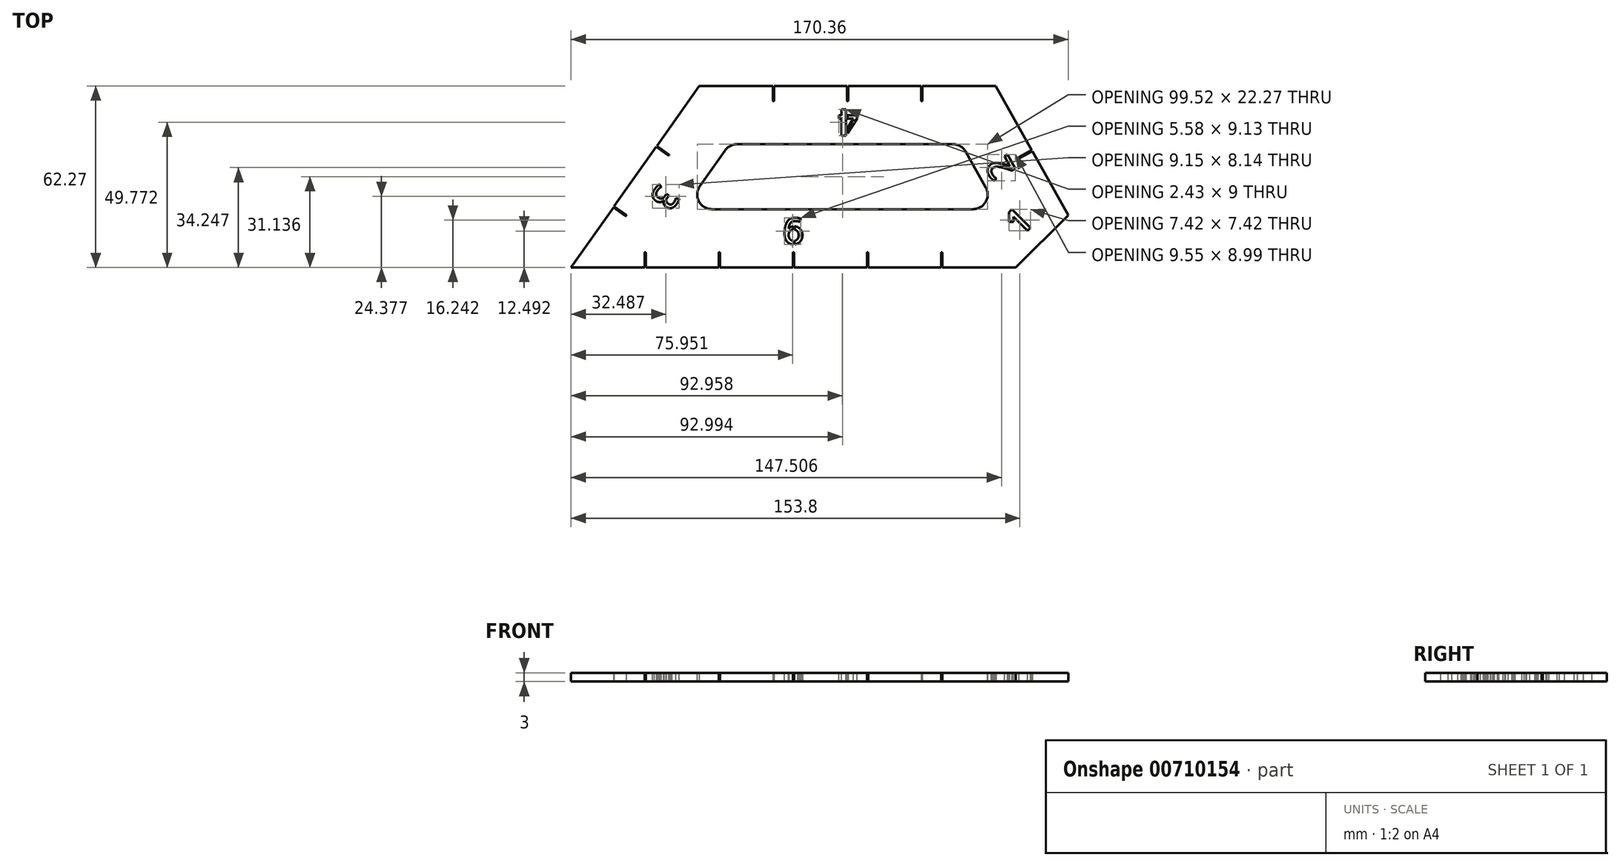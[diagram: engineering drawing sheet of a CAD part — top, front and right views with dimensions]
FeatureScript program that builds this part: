
annotation { "Feature Type Name" : "Feature", "Feature Type Description" : "" }
export const myFeature = defineFeature(function(context is Context, id is Id, definition is map)
    precondition{}
    {
        {
            var Q0;
            Q0=qCreatedBy(makeId("Top.planeOp"),FACE);
            var sketch = newSketch(context, id + "F0", { "sketchPlane" : qUnion([Q0])});
            skLineSegment(sketch, "E0.0.0", {"start": v(145.52, 62.27) * mm, "end": v(43.92, 62.27) * mm});
            skLineSegment(sketch, "E0.0.1", {"start": v(43.92, 62.27) * mm, "end": v(0, 0) * mm});
            skLineSegment(sketch, "E0.0.2", {"start": v(0, 0) * mm, "end": v(152.4, 0) * mm});
            skLineSegment(sketch, "E0.0.3", {"start": v(152.4, 0) * mm, "end": v(170.36, 17.96) * mm});
            skLineSegment(sketch, "E0.0.4", {"start": v(170.36, 17.96) * mm, "end": v(145.52, 62.27) * mm});
            skLineSegment(sketch, "E1", {"start": v(25.4, 0) * mm, "end": v(25.4, 5) * mm, "construction": true});
            skLineSegment(sketch, "E2.1.0.0", {"start": v(50.8, 0) * mm, "end": v(50.8, 5) * mm, "construction": true});
            skLineSegment(sketch, "E2.2.0.0", {"start": v(76.2, 0) * mm, "end": v(76.2, 5) * mm, "construction": true});
            skLineSegment(sketch, "E2.3.0.0", {"start": v(101.6, 0) * mm, "end": v(101.6, 5) * mm, "construction": true});
            skLineSegment(sketch, "E2.4.0.0", {"start": v(127, 0) * mm, "end": v(127, 5) * mm, "construction": true});
            skLineSegment(sketch, "E2.direction1", {"start": v(25.4, 0) * mm, "end": v(50.8, 0) * mm, "construction": true});
            skArc(sketch, "E3.0.startCap", {"start": v(25.6, 0) * mm, "mid": v(25.4, -0.2) * mm, "end": v(25.2, 0) * mm});
            skArc(sketch, "E3.0.endCap", {"start": v(25.2, 5) * mm, "mid": v(25.4, 5.2) * mm, "end": v(25.6, 5) * mm});
            skLineSegment(sketch, "E3.0.left", {"start": v(25.2, 0) * mm, "end": v(25.2, 5) * mm});
            skLineSegment(sketch, "E3.0.right", {"start": v(25.6, 0) * mm, "end": v(25.6, 5) * mm});
            skArc(sketch, "E3.1.startCap", {"start": v(51, 0) * mm, "mid": v(50.8, -0.2) * mm, "end": v(50.6, 0) * mm});
            skArc(sketch, "E3.1.endCap", {"start": v(50.6, 5) * mm, "mid": v(50.8, 5.2) * mm, "end": v(51, 5) * mm});
            skLineSegment(sketch, "E3.1.left", {"start": v(50.6, 0) * mm, "end": v(50.6, 5) * mm});
            skLineSegment(sketch, "E3.1.right", {"start": v(51, 0) * mm, "end": v(51, 5) * mm});
            skArc(sketch, "E3.2.startCap", {"start": v(76.4, 0) * mm, "mid": v(76.2, -0.2) * mm, "end": v(76, 0) * mm});
            skArc(sketch, "E3.2.endCap", {"start": v(76, 5) * mm, "mid": v(76.2, 5.2) * mm, "end": v(76.4, 5) * mm});
            skLineSegment(sketch, "E3.2.left", {"start": v(76, 0) * mm, "end": v(76, 5) * mm});
            skLineSegment(sketch, "E3.2.right", {"start": v(76.4, 0) * mm, "end": v(76.4, 5) * mm});
            skArc(sketch, "E3.3.startCap", {"start": v(101.8, 0) * mm, "mid": v(101.6, -0.2) * mm, "end": v(101.4, 0) * mm});
            skArc(sketch, "E3.3.endCap", {"start": v(101.4, 5) * mm, "mid": v(101.6, 5.2) * mm, "end": v(101.8, 5) * mm});
            skLineSegment(sketch, "E3.3.left", {"start": v(101.4, 0) * mm, "end": v(101.4, 5) * mm});
            skLineSegment(sketch, "E3.3.right", {"start": v(101.8, 0) * mm, "end": v(101.8, 5) * mm});
            skArc(sketch, "E3.4.startCap", {"start": v(127.2, 0) * mm, "mid": v(127, -0.2) * mm, "end": v(126.8, 0) * mm});
            skArc(sketch, "E3.4.endCap", {"start": v(126.8, 5) * mm, "mid": v(127, 5.2) * mm, "end": v(127.2, 5) * mm});
            skLineSegment(sketch, "E3.4.left", {"start": v(126.8, 0) * mm, "end": v(126.8, 5) * mm});
            skLineSegment(sketch, "E3.4.right", {"start": v(127.2, 0) * mm, "end": v(127.2, 5) * mm});
            skLineSegment(sketch, "E4", {"start": v(157.94, 40.12) * mm, "end": v(153.58, 37.67) * mm, "construction": true});
            skLineSegment(sketch, "E5", {"start": v(69.32, 62.27) * mm, "end": v(69.32, 57.27) * mm, "construction": true});
            skLineSegment(sketch, "E6", {"start": v(14.64, 20.76) * mm, "end": v(18.73, 17.88) * mm, "construction": true});
            skArc(sketch, "E7.0.startCap", {"start": v(14.52, 20.6) * mm, "mid": v(14.48, 20.87) * mm, "end": v(14.75, 20.92) * mm});
            skArc(sketch, "E7.0.endCap", {"start": v(18.84, 18.04) * mm, "mid": v(18.89, 17.76) * mm, "end": v(18.6, 17.71) * mm});
            skLineSegment(sketch, "E7.0.left", {"start": v(14.75, 20.92) * mm, "end": v(18.84, 18.04) * mm});
            skLineSegment(sketch, "E7.0.right", {"start": v(14.52, 20.6) * mm, "end": v(18.6, 17.71) * mm});
            skArc(sketch, "E7.1.startCap", {"start": v(69.12, 62.27) * mm, "mid": v(69.32, 62.47) * mm, "end": v(69.52, 62.27) * mm});
            skArc(sketch, "E7.1.endCap", {"start": v(69.52, 57.27) * mm, "mid": v(69.32, 57.07) * mm, "end": v(69.12, 57.27) * mm});
            skLineSegment(sketch, "E7.1.left", {"start": v(69.52, 62.27) * mm, "end": v(69.52, 57.27) * mm});
            skLineSegment(sketch, "E7.1.right", {"start": v(69.12, 62.27) * mm, "end": v(69.12, 57.27) * mm});
            skArc(sketch, "E7.2.startCap", {"start": v(157.84, 40.3) * mm, "mid": v(158.11, 40.21) * mm, "end": v(158.04, 39.94) * mm});
            skArc(sketch, "E7.2.endCap", {"start": v(153.68, 37.5) * mm, "mid": v(153.4, 37.57) * mm, "end": v(153.48, 37.85) * mm});
            skLineSegment(sketch, "E7.2.left", {"start": v(158.04, 39.94) * mm, "end": v(153.68, 37.5) * mm});
            skLineSegment(sketch, "E7.2.right", {"start": v(157.84, 40.3) * mm, "end": v(153.48, 37.85) * mm});
            skLineSegment(sketch, "E8.1.0.0", {"start": v(29.4, 41.68) * mm, "end": v(33.48, 38.8) * mm});
            skLineSegment(sketch, "E8.1.0.1", {"start": v(29.16, 41.35) * mm, "end": v(33.25, 38.47) * mm});
            skLineSegment(sketch, "E8.1.0.2", {"start": v(29.28, 41.51) * mm, "end": v(33.36, 38.63) * mm, "construction": true});
            skArc(sketch, "E8.1.0.3", {"start": v(29.16, 41.35) * mm, "mid": v(29.11, 41.63) * mm, "end": v(29.4, 41.68) * mm});
            skArc(sketch, "E8.1.0.4", {"start": v(33.48, 38.8) * mm, "mid": v(33.53, 38.52) * mm, "end": v(33.25, 38.47) * mm});
            skLineSegment(sketch, "E8.direction1", {"start": v(14.52, 20.6) * mm, "end": v(29.16, 41.35) * mm, "construction": true});
            skLineSegment(sketch, "E9.1.0.0", {"start": v(94.52, 62.27) * mm, "end": v(94.52, 57.27) * mm});
            skLineSegment(sketch, "E9.1.0.1", {"start": v(94.92, 62.27) * mm, "end": v(94.92, 57.27) * mm});
            skLineSegment(sketch, "E9.1.0.2", {"start": v(94.72, 62.27) * mm, "end": v(94.72, 57.27) * mm, "construction": true});
            skArc(sketch, "E9.1.0.3", {"start": v(94.52, 62.27) * mm, "mid": v(94.72, 62.47) * mm, "end": v(94.92, 62.27) * mm});
            skArc(sketch, "E9.1.0.4", {"start": v(94.92, 57.27) * mm, "mid": v(94.72, 57.07) * mm, "end": v(94.52, 57.27) * mm});
            skLineSegment(sketch, "E9.2.0.0", {"start": v(119.92, 62.27) * mm, "end": v(119.92, 57.27) * mm});
            skLineSegment(sketch, "E9.2.0.1", {"start": v(120.32, 62.27) * mm, "end": v(120.32, 57.27) * mm});
            skLineSegment(sketch, "E9.2.0.2", {"start": v(120.12, 62.27) * mm, "end": v(120.12, 57.27) * mm, "construction": true});
            skArc(sketch, "E9.2.0.3", {"start": v(119.92, 62.27) * mm, "mid": v(120.12, 62.47) * mm, "end": v(120.32, 62.27) * mm});
            skArc(sketch, "E9.2.0.4", {"start": v(120.32, 57.27) * mm, "mid": v(120.12, 57.07) * mm, "end": v(119.92, 57.27) * mm});
            skLineSegment(sketch, "E9.direction1", {"start": v(69.12, 57.27) * mm, "end": v(94.52, 57.27) * mm, "construction": true});
            skLineSegment(sketch, "E10", {"start": v(38.58, 20) * mm, "end": v(54.29, 42.27) * mm});
            skLineSegment(sketch, "E11", {"start": v(54.29, 42.27) * mm, "end": v(133.8, 42.27) * mm});
            skLineSegment(sketch, "E12", {"start": v(133.8, 42.27) * mm, "end": v(146.29, 20) * mm});
            skLineSegment(sketch, "E13", {"start": v(146.29, 20) * mm, "end": v(38.58, 20) * mm});
            skSolve(sketch);
        }
        {
            var Q0;
            {var subQ33=sQuery(id+"F0.wireOp",EDGE,"E0.0.3");Q0=makeQuery(id+"F0.imprint","IMPRINT",FACE,{"disambiguationData":[TD([[makeQuery(id+"F0.imprint","IMPRINT",EDGE,{"derivedFrom":subQ33}),1.0]])]});}
            extrude(context, id + "F1", {"entities" : qUnion([Q0]), "depth" : 3 * mm, "offsetDistance" : 25 * mm});
        }
        {
            var Q0;
            Q0=makeQuery(id+"F1.opExtrude","SWEPT_EDGE",EDGE,{"disambiguationData":[OSD([sQuery(id+"F0.wireOp",EDGE,"E10"),sQuery(id+"F0.wireOp",EDGE,"E11")])]});
            var Q1;
            Q1=makeQuery(id+"F1.opExtrude","SWEPT_EDGE",EDGE,{"disambiguationData":[OSD([sQuery(id+"F0.wireOp",EDGE,"E10"),sQuery(id+"F0.wireOp",EDGE,"E13")])]});
            var Q2;
            Q2=makeQuery(id+"F1.opExtrude","SWEPT_EDGE",EDGE,{"disambiguationData":[OSD([sQuery(id+"F0.wireOp",EDGE,"E11"),sQuery(id+"F0.wireOp",EDGE,"E12")])]});
            var Q3;
            Q3=makeQuery(id+"F1.opExtrude","SWEPT_EDGE",EDGE,{"disambiguationData":[OSD([sQuery(id+"F0.wireOp",EDGE,"E12"),sQuery(id+"F0.wireOp",EDGE,"E13")])]});
            fillet(context, id + "F2", {"entities" : qUnion([Q0, Q1, Q2, Q3]), "radius" : 5 * mm, "tangentPropagation" : true, "allowEdgeOverflow" : false});
        }
        {
            var Q0;
            Q0=makeQuery(id+"F1.opExtrude","CAP_FACE",FACE,{"disambiguationData":[OSD([sQuery(id+"F0.wireOp",EDGE,"E0.0.0"),sQuery(id+"F0.wireOp",EDGE,"E0.0.1"),sQuery(id+"F0.wireOp",EDGE,"E0.0.2"),sQuery(id+"F0.wireOp",EDGE,"E0.0.3"),sQuery(id+"F0.wireOp",EDGE,"E0.0.4"),sQuery(id+"F0.wireOp",EDGE,"E3.0.endCap"),sQuery(id+"F0.wireOp",EDGE,"E3.0.left"),sQuery(id+"F0.wireOp",EDGE,"E3.0.right"),sQuery(id+"F0.wireOp",EDGE,"E3.1.endCap"),sQuery(id+"F0.wireOp",EDGE,"E3.1.left"),sQuery(id+"F0.wireOp",EDGE,"E3.1.right"),sQuery(id+"F0.wireOp",EDGE,"E3.2.endCap"),sQuery(id+"F0.wireOp",EDGE,"E3.2.left"),sQuery(id+"F0.wireOp",EDGE,"E3.2.right"),sQuery(id+"F0.wireOp",EDGE,"E3.3.endCap"),sQuery(id+"F0.wireOp",EDGE,"E3.3.left"),sQuery(id+"F0.wireOp",EDGE,"E3.3.right"),sQuery(id+"F0.wireOp",EDGE,"E3.4.endCap"),sQuery(id+"F0.wireOp",EDGE,"E3.4.left"),sQuery(id+"F0.wireOp",EDGE,"E3.4.right"),sQuery(id+"F0.wireOp",EDGE,"E7.0.endCap"),sQuery(id+"F0.wireOp",EDGE,"E7.0.left"),sQuery(id+"F0.wireOp",EDGE,"E7.0.right"),sQuery(id+"F0.wireOp",EDGE,"E7.1.endCap"),sQuery(id+"F0.wireOp",EDGE,"E7.1.left"),sQuery(id+"F0.wireOp",EDGE,"E7.1.right"),sQuery(id+"F0.wireOp",EDGE,"E7.2.endCap"),sQuery(id+"F0.wireOp",EDGE,"E7.2.left"),sQuery(id+"F0.wireOp",EDGE,"E7.2.right"),sQuery(id+"F0.wireOp",EDGE,"E8.1.0.0"),sQuery(id+"F0.wireOp",EDGE,"E8.1.0.1"),sQuery(id+"F0.wireOp",EDGE,"E8.1.0.4"),sQuery(id+"F0.wireOp",EDGE,"E9.1.0.0"),sQuery(id+"F0.wireOp",EDGE,"E9.1.0.1"),sQuery(id+"F0.wireOp",EDGE,"E9.1.0.4"),sQuery(id+"F0.wireOp",EDGE,"E9.2.0.0"),sQuery(id+"F0.wireOp",EDGE,"E9.2.0.1"),sQuery(id+"F0.wireOp",EDGE,"E9.2.0.4"),sQuery(id+"F0.wireOp",EDGE,"E10"),sQuery(id+"F0.wireOp",EDGE,"E11"),sQuery(id+"F0.wireOp",EDGE,"E12"),sQuery(id+"F0.wireOp",EDGE,"E13")])],"isStart":false});
            var sketch = newSketch(context, id + "F3", { "sketchPlane" : qUnion([Q0])});
            skText(sketch, "E14", { "text": "6", "fontName": "AllertaStencil-Regular.ttf"});
            skText(sketch, "E15", { "text": "3", "fontName": "AllertaStencil-Regular.ttf"});
            skText(sketch, "E16", { "text": "4", "fontName": "AllertaStencil-Regular.ttf"});
            skText(sketch, "E17", { "text": "1", "fontName": "AllertaStencil-Regular.ttf"});
            skText(sketch, "E18", { "text": "2", "fontName": "AllertaStencil-Regular.ttf"});
            skPoint(sketch, "E19", {"position": v(160.58, 8.18) * mm});
            skLineSegment(sketch, "E20", {"start": v(160.58, 8.18) * mm, "end": v(156.34, 12.43) * mm, "construction": true});
            skLineSegment(sketch, "E21", {"start": v(150.96, 36.2) * mm, "end": v(153.4, 37.57) * mm, "construction": true});
            skLineSegment(sketch, "E22", {"start": v(28.5, 26.52) * mm, "end": v(21.96, 31.14) * mm, "construction": true});
            skLineSegment(sketch, "E23", {"start": v(94.72, 54.27) * mm, "end": v(94.72, 57.47) * mm, "construction": true});
            skPoint(sketch, "E24", {"position": v(76.2, 5.2) * mm});
            const initialGuessF3  = {"E14": [0.07227, 0.008, 1, 0, 0.009], "E15": [0.03053, 0.0294, -0.57634, -0.8172, 0.009], "E16": [0.09853, 0.05427, -1, 0, 0.009], "E17": [0.15459, 0.01067, 0.7071, 0.7071, 0.009], "E18": [0.1528, 0.03294, -0.48904, 0.87226, 0.009]};
            skSetInitialGuess(sketch, initialGuessF3);
            skSolve(sketch);
        }
        {
            var Q0;
            Q0 = qSketchRegion(id + "F3", true);
            extrude(context, id + "F4", {"entities" : qUnion([Q0]), "operationType" : NewBodyOperationType.REMOVE, "endBound" : BoundingType.UP_TO_NEXT, "oppositeDirection" : true, "depth" : .9 * mm, "offsetDistance" : 25 * mm});
        }
    });
